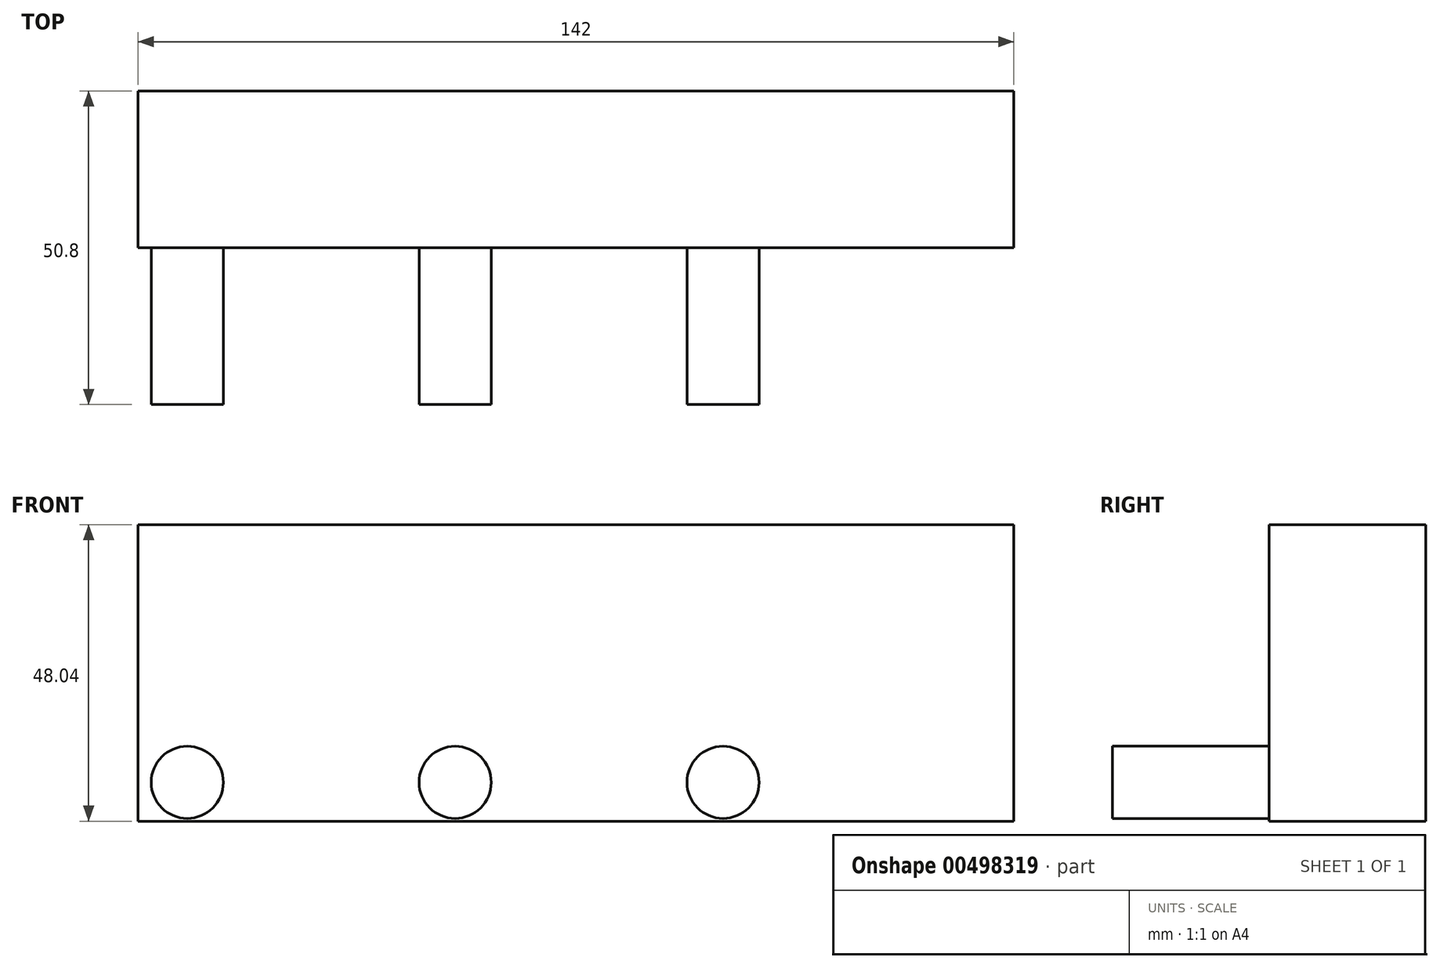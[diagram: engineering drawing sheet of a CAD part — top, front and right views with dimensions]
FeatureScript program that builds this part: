
annotation { "Feature Type Name" : "Feature", "Feature Type Description" : "" }
export const myFeature = defineFeature(function(context is Context, id is Id, definition is map)
    precondition{}
    {
        {
            var Q0;
            Q0=qCreatedBy(makeId("Front.planeOp"),FACE);
            var sketch = newSketch(context, id + "F0", { "sketchPlane" : qUnion([Q0])});
            skLineSegment(sketch, "E0.bottom", {"start": v(-69.2, 52) * mm, "end": v(72.8, 52) * mm});
            skLineSegment(sketch, "E0.top", {"start": v(-69.2, 3.96) * mm, "end": v(72.8, 3.96) * mm});
            skLineSegment(sketch, "E0.left", {"start": v(-69.2, 52) * mm, "end": v(-69.2, 3.96) * mm});
            skLineSegment(sketch, "E0.right", {"start": v(72.8, 52) * mm, "end": v(72.8, 3.96) * mm});
            skSolve(sketch);
        }
        {
            var Q0;
            Q0 = qSketchRegion(id + "F0", true);
            extrude(context, id + "F1", {"entities" : qUnion([Q0]), "depth" : 25.4 * mm});
        }
        {
            var Q0;
            Q0=makeQuery(id+"F1.opExtrude","CAP_FACE",FACE,{"disambiguationData":[OSD([sQuery(id+"F0.wireOp",EDGE,"E0.bottom"),sQuery(id+"F0.wireOp",EDGE,"E0.top"),sQuery(id+"F0.wireOp",EDGE,"E0.left"),sQuery(id+"F0.wireOp",EDGE,"E0.right")])],"isStart":false});
            var sketch = newSketch(context, id + "F2", { "sketchPlane" : qUnion([Q0])});
            skCircle(sketch, "E1", {"center": v(-61.22, 10.25) * mm, "radius": 5.85 * mm});
            skCircle(sketch, "E2.1.0.0", {"center": v(-17.78, 10.25) * mm, "radius": 5.85 * mm});
            skCircle(sketch, "E2.2.0.0", {"center": v(25.65, 10.25) * mm, "radius": 5.85 * mm});
            skLineSegment(sketch, "E2.direction1", {"start": v(-61.22, 10.25) * mm, "end": v(-17.78, 10.25) * mm, "construction": true});
            skSolve(sketch);
        }
        {
            var Q0;
            Q0=makeQuery(id+"F2.imprint","IMPRINT",FACE,{"disambiguationData":[TD([[makeQuery(id+"F2.imprint","IMPRINT",EDGE,{"derivedFrom":sQuery(id+"F2.wireOp",EDGE,"E1")}),1.0]])]});
            var Q1;
            Q1 = qSketchRegion(id + "F2", true);
            extrude(context, id + "F3", {"entities" : qUnion([Q0, Q1]), "operationType" : NewBodyOperationType.ADD, "depth" : 25.4 * mm});
        }
    });
